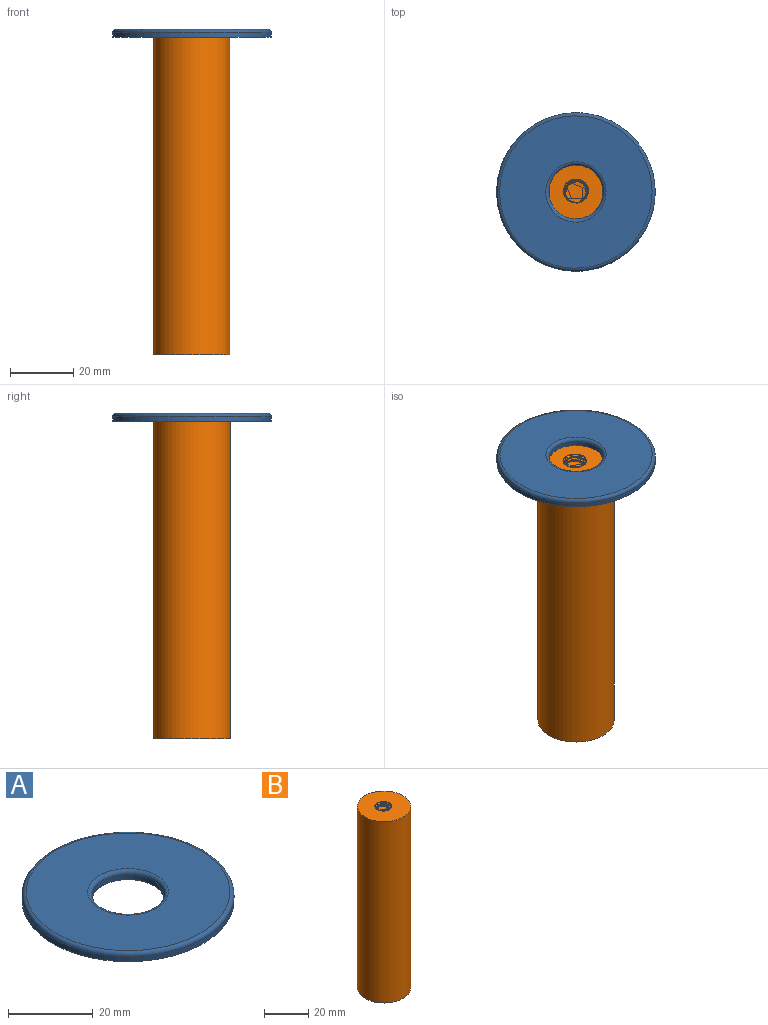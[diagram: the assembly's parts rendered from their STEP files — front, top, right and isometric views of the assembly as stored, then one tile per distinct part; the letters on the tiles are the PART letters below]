
ASSEMBLY  parts=2 mates=1
PART A: 6 faces, bbox 54.1x54.1x2.5 mm
  f0: cylinder r=8.5mm len=17mm, axis (0,0,-1), area 80.1mm2, adj f3,f4
  f1: cylinder r=25mm len=50mm, axis (0,0,-1), area 235.6mm2, adj f3,f5
  f2: plane 48x48mm, normal (0,0,1), area 1526mm2, adj f4,f5
  f3: plane 50x50mm, normal (0,0,-1), area 1736.5mm2, adj f0,f1
  f4: torus R=9.5mm, axis (0,0,1), area 87.5mm2, adj f0,f2
  f5: torus R=24mm, axis (0,0,1), area 243.2mm2, adj f1,f2
PART B: 8 faces, bbox 24.4x24.4x100.9 mm
  f0: plane 7.7x7.69mm, normal (0,0,1), area 42.6mm2, adj f4,f5,f6,f7
  f1: plane 24.36x24.36mm, normal (0,0,1), area 409.8mm2, adj f2,f4,f5,f6,f7
  f2: cylinder r=12mm len=100mm, axis (0,0,-1), area 7539.8mm2, adj f1,f3
  f3: plane 24x24mm, normal (0,0,-1), area 452.4mm2, adj f2
  f4: bspline ~25.81x9.36mm, area 362.7mm2, adj f0,f1,f6,f7
  f5: bspline ~26.02x9.36mm, area 366.4mm2, adj f0,f1,f6,f7
  f6: bspline ~25.57x9.49mm, area 92.5mm2, adj f0,f1,f4,f5
  f7: cylinder r=3.38mm len=25mm, axis (0,0,-1), area 307.5mm2, adj f0,f1,f4,f5
PLACE A t=(0,0,100)mm
PLACE B at identity
MATE planar A.f1 <-> B.f2  axis (0,0,-1) through (0,0,100)mm
